# Revit family: E1506UPM
name_source: partatom
category: Lighting Fixtures
revit_build: Autodesk Revit 2017 (Build: 20160225_1515(x64)
units: mm (PartAtom-declared; Revit-internal decimal feet)

## family parameters
Cut with Voids When Loaded = No
Host = Face
Light Source = Yes
Part Type = Normal
Room Calculation Point = No
Round Connector Dimension = Use Diameter
Shared = No

## types (2) — shared parameters
Apparent Load = 45 VA
Color Filter = 16777215
Default Elevation = 1219 mm
Dimming Lamp Color Temperature Shift = <None>
Emit Shape Visible in Rendering = No
Emit from Rectangle Length = 1550 mm  [stored 5.0853 ft]
Emit from Rectangle Width = 100 mm  [stored 0.328084 ft]
Lamp = LED
Manufacturer = ARLIGHT
Model = E1206UPM
Photometric Web File = E 1206 UPM-36W-4K(SG).IES
Tilt Angle = -90.00°
Type Comments = Industrial Lighting
Type Image = 1206.jpg
URL = http://www.arlight.net
Wattage Comments = 45W

## type names (no varying parameters)
- EUPM.1506.45.30
- EUPM.1506.45.40

note: [stored X ft] marks values corroborated as IEEE doubles in the binary element streams (Revit-internal decimal feet)

## geometry (parser evidence)
native form markers: Sweep x3
no freeform markers — native parametric forms only
